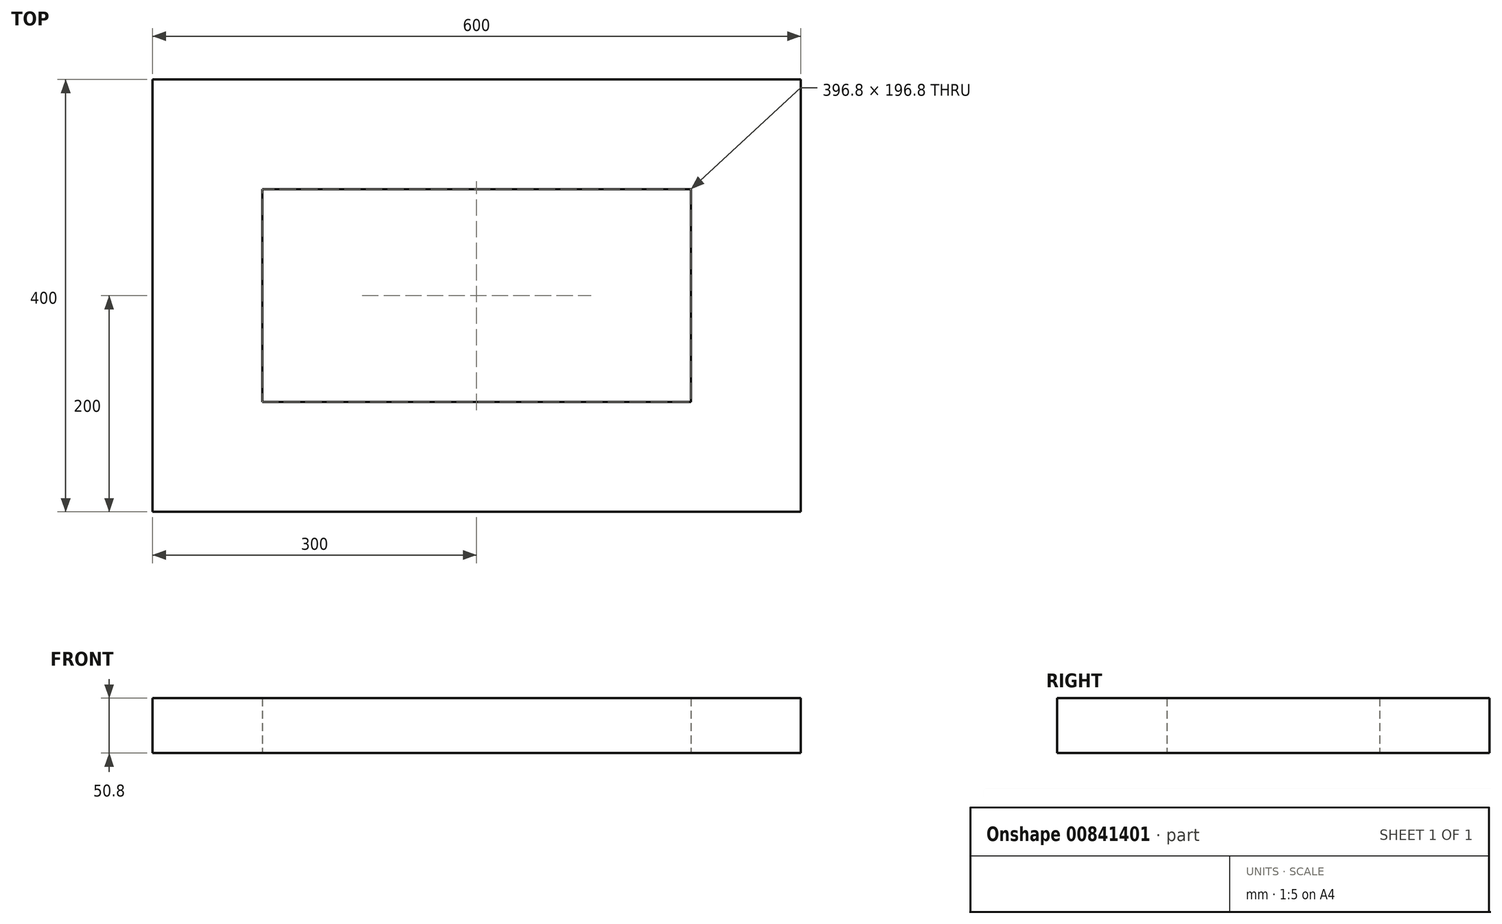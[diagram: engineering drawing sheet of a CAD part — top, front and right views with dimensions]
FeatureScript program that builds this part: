
annotation { "Feature Type Name" : "Feature", "Feature Type Description" : "" }
export const myFeature = defineFeature(function(context is Context, id is Id, definition is map)
    precondition{}
    {
        {
            var Q0;
            Q0=qCreatedBy(makeId("Top.planeOp"),FACE);
            var sketch = newSketch(context, id + "F0", { "sketchPlane" : qUnion([Q0])});
            skLineSegment(sketch, "E0.bottom", {"start": v(0, 0) * mm, "end": v(600, 0) * mm});
            skLineSegment(sketch, "E0.top", {"start": v(0, 400) * mm, "end": v(600, 400) * mm});
            skLineSegment(sketch, "E0.left", {"start": v(0, 0) * mm, "end": v(0, 400) * mm});
            skLineSegment(sketch, "E0.right", {"start": v(600, 0) * mm, "end": v(600, 400) * mm});
            skLineSegment(sketch, "E1.bottom", {"start": v(101.6, 298.4) * mm, "end": v(498.4, 298.4) * mm});
            skLineSegment(sketch, "E1.top", {"start": v(101.6, 101.6) * mm, "end": v(498.4, 101.6) * mm});
            skLineSegment(sketch, "E1.left", {"start": v(101.6, 298.4) * mm, "end": v(101.6, 101.6) * mm});
            skLineSegment(sketch, "E1.right", {"start": v(498.4, 298.4) * mm, "end": v(498.4, 101.6) * mm});
            skSolve(sketch);
        }
        {
            var Q0;
            Q0=makeQuery(id+"F0.imprint","IMPRINT",FACE,{"disambiguationData":[TD([[makeQuery(id+"F0.imprint","IMPRINT",EDGE,{"derivedFrom":sQuery(id+"F0.wireOp",EDGE,"E0.bottom")}),1.0]])]});
            extrude(context, id + "F1", {"entities" : qUnion([Q0]), "depth" : 50.8 * mm, "offsetDistance" : 25 * mm});
        }
    });
